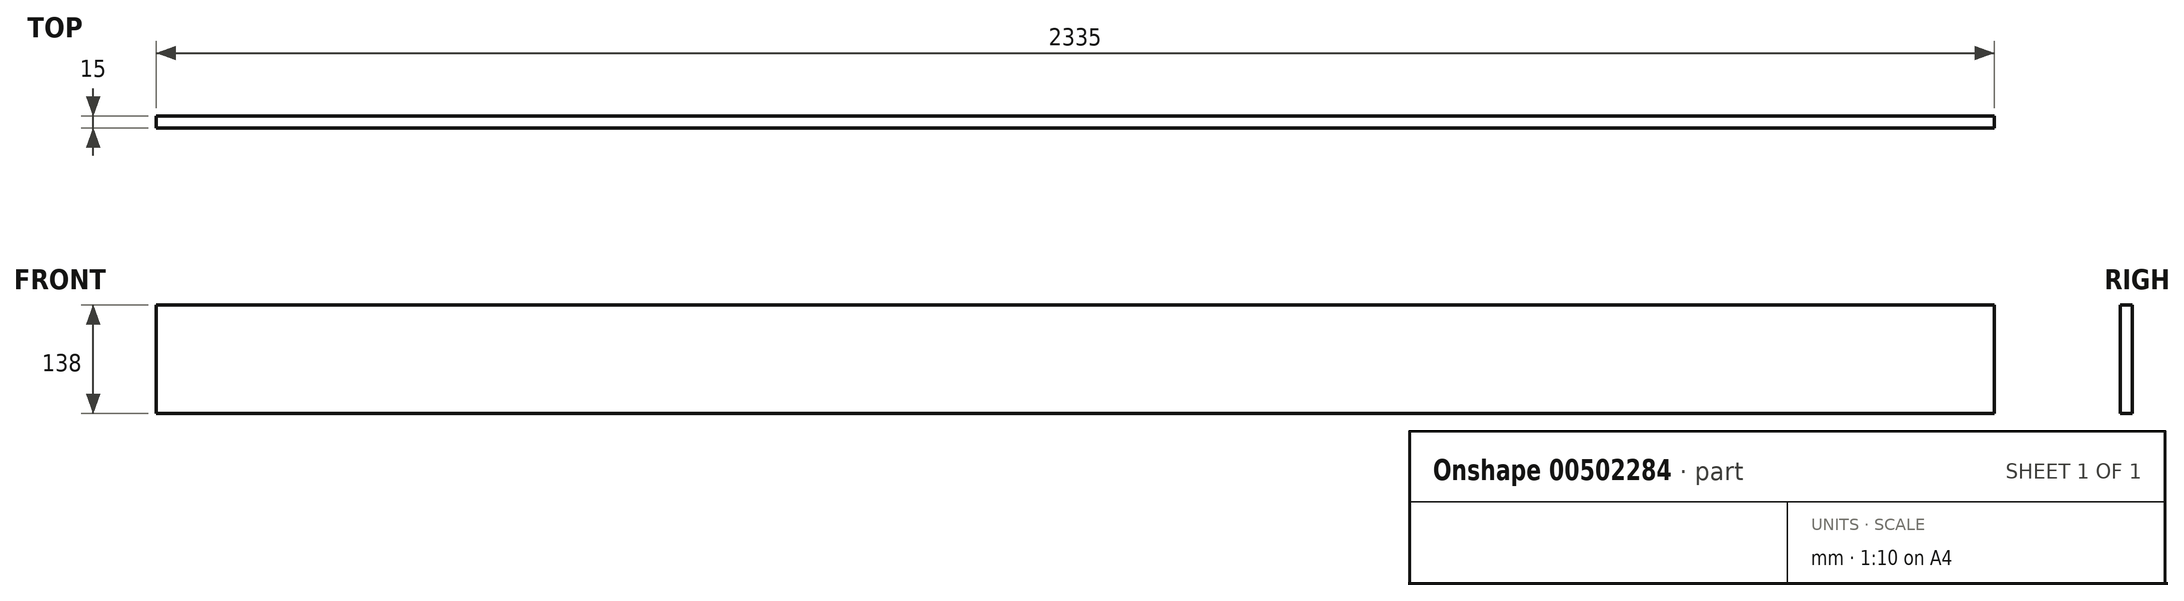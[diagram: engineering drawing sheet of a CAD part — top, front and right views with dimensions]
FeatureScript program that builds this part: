
annotation { "Feature Type Name" : "Feature", "Feature Type Description" : "" }
export const myFeature = defineFeature(function(context is Context, id is Id, definition is map)
    precondition{}
    {
        {
            var Q0;
            Q0=qCreatedBy(makeId("Front.planeOp"),FACE);
            var sketch = newSketch(context, id + "F0", { "sketchPlane" : qUnion([Q0])});
            skLineSegment(sketch, "E0.bottom", {"start": v(-1000, 69) * mm, "end": v(1335, 69) * mm});
            skLineSegment(sketch, "E0.top", {"start": v(-1000, -69) * mm, "end": v(1335, -69) * mm});
            skLineSegment(sketch, "E0.left", {"start": v(-1000, 69) * mm, "end": v(-1000, -69) * mm});
            skLineSegment(sketch, "E0.right", {"start": v(1335, 69) * mm, "end": v(1335, -69) * mm});
            skSolve(sketch);
        }
        {
            var Q0;
            Q0 = qSketchRegion(id + "F0", true);
            extrude(context, id + "F1", {"entities" : qUnion([Q0]), "depth" : 15 * mm});
        }
    });
